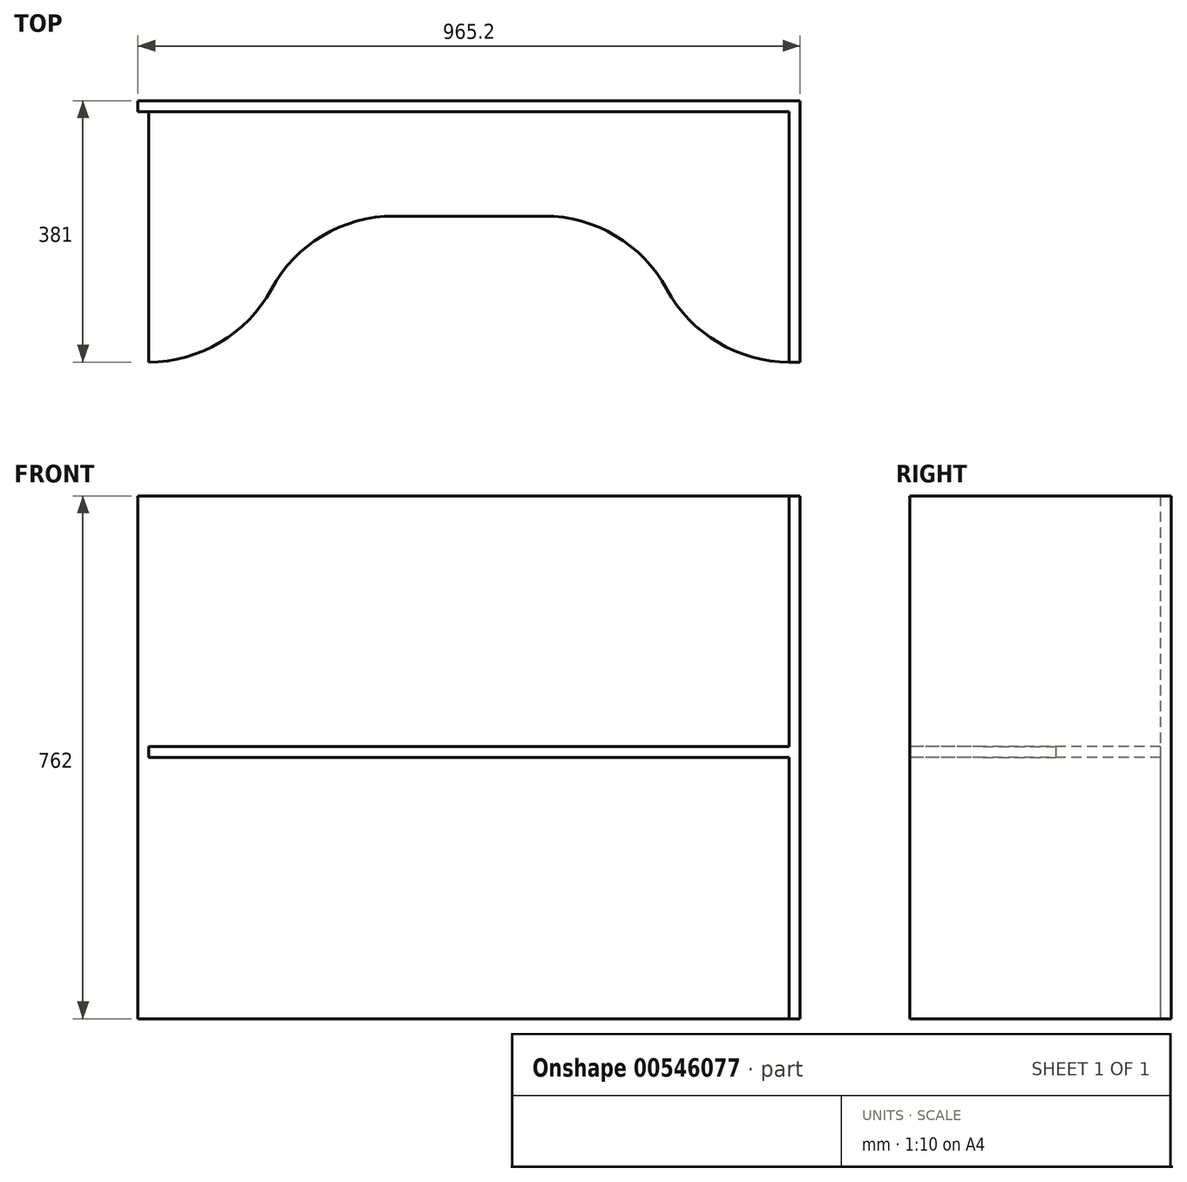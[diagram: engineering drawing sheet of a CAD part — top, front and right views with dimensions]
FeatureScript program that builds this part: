
annotation { "Feature Type Name" : "Feature", "Feature Type Description" : "" }
export const myFeature = defineFeature(function(context is Context, id is Id, definition is map)
    precondition{}
    {
        {
            var Q0;
            Q0=qCreatedBy(makeId("Front.planeOp"),FACE);
            var sketch = newSketch(context, id + "F0", { "sketchPlane" : qUnion([Q0])});
            skLineSegment(sketch, "E0.bottom", {"start": v(-482.6, 381) * mm, "end": v(482.6, 381) * mm});
            skLineSegment(sketch, "E0.top", {"start": v(-482.6, -381) * mm, "end": v(482.6, -381) * mm});
            skLineSegment(sketch, "E0.left", {"start": v(-482.6, 381) * mm, "end": v(-482.6, -381) * mm});
            skLineSegment(sketch, "E0.right", {"start": v(482.6, 381) * mm, "end": v(482.6, -381) * mm});
            skPoint(sketch, "E0.middle", {"position": v(0, 0) * mm});
            skSolve(sketch);
        }
        {
            var Q0;
            Q0=makeQuery(id+"F0.imprint","IMPRINT",FACE,{"disambiguationData":[TD([[makeQuery(id+"F0.imprint","IMPRINT",EDGE,{"derivedFrom":sQuery(id+"F0.wireOp",EDGE,"E0.bottom")}),-1.0]])]});
            extrude(context, id + "F1", {"entities" : qUnion([Q0]), "oppositeDirection" : true, "depth" : 15.88 * mm, "offsetDistance" : 25.4 * mm});
        }
        {
            var Q0;
            Q0=makeQuery(id+"F1.opExtrude","SWEPT_FACE",FACE,{"disambiguationData":[OSD([sQuery(id+"F0.wireOp",EDGE,"E0.right")])]});
            var sketch = newSketch(context, id + "F2", { "sketchPlane" : qUnion([Q0])});
            skLineSegment(sketch, "E1.bottom", {"start": v(0, 381) * mm, "end": v(-365.13, 381) * mm});
            skLineSegment(sketch, "E1.top", {"start": v(0, -381) * mm, "end": v(-365.12, -381) * mm});
            skLineSegment(sketch, "E1.left", {"start": v(0, 381) * mm, "end": v(0, -381) * mm});
            skLineSegment(sketch, "E1.right", {"start": v(-365.13, 381) * mm, "end": v(-365.12, -381) * mm});
            skSolve(sketch);
        }
        {
            var Q0;
            Q0=makeQuery(id+"F2.imprint","IMPRINT",FACE,{"disambiguationData":[TD([[makeQuery(id+"F2.imprint","IMPRINT",EDGE,{"derivedFrom":sQuery(id+"F2.wireOp",EDGE,"E1.bottom")}),1.0]])]});
            extrude(context, id + "F3", {"entities" : qUnion([Q0]), "oppositeDirection" : true, "depth" : 15.88 * mm, "offsetDistance" : 25.4 * mm});
        }
        {
            var Q0;
            Q0=qCreatedBy(makeId("Top.planeOp"),FACE);
            var sketch = newSketch(context, id + "F4", { "sketchPlane" : qUnion([Q0])});
            skLineSegment(sketch, "E2.0", {"start": v(466.73, -365.13) * mm, "end": v(482.6, -365.13) * mm});
            skLineSegment(sketch, "E3.0", {"start": v(466.73, 0) * mm, "end": v(466.73, -365.13) * mm});
            skLineSegment(sketch, "E4.0", {"start": v(-482.6, 0) * mm, "end": v(482.6, 0) * mm});
            skArc(sketch, "E5", {"start": v(466.73, -365.13) * mm, "mid": v(362.77, -336.52) * mm, "end": v(288.08, -258.76) * mm});
            skArc(sketch, "E6", {"start": v(288.08, -258.76) * mm, "mid": v(213.4, -181) * mm, "end": v(109.44, -152.4) * mm});
            skLineSegment(sketch, "E7", {"start": v(109.44, -152.4) * mm, "end": v(0, -152.4) * mm});
            skLineSegment(sketch, "E8", {"start": v(0, -152.4) * mm, "end": v(0, 0) * mm});
            skSolve(sketch);
        }
        {
            var Q0;
            {var subQ1=sQuery(id+"F4.wireOp",EDGE,"E3.0");Q0=makeQuery(id+"F4.imprint","IMPRINT",FACE,{"disambiguationData":[TD([[makeQuery(id+"F4.imprint","IMPRINT",EDGE,{"derivedFrom":subQ1}),-1.0]])]});}
            extrude(context, id + "F5", {"entities" : qUnion([Q0]), "depth" : 15.88 * mm, "offsetDistance" : 25.4 * mm});
        }
        {
            var Q0;
            Q0=makeQuery(id+"F5.opExtrude","SWEPT_BODY",BODY,{"disambiguationData":[OSD([sQuery(id+"F4.wireOp",EDGE,"E3.0"),sQuery(id+"F4.wireOp",EDGE,"E4.0"),sQuery(id+"F4.wireOp",EDGE,"E5"),sQuery(id+"F4.wireOp",EDGE,"E6"),sQuery(id+"F4.wireOp",EDGE,"E7"),sQuery(id+"F4.wireOp",EDGE,"E8")])]});
            var Q1;
            Q1=qCreatedBy(makeId("Right.planeOp"),FACE);
            mirror(context, id + "F6", {"operationType" : NewBodyOperationType.ADD, "entities" : qUnion([Q0]), "mirrorPlane" : qUnion([Q1])});
        }
    });
